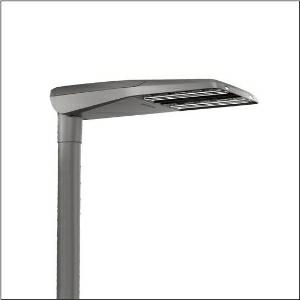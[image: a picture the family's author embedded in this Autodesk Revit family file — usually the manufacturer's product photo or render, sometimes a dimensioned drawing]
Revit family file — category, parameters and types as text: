
# Revit family: streetlight_sl_11_iq_midi___st1_2a_5xc3a41f08me_055e
name_source: partatom
category: Lighting Fixtures
units: mm (PartAtom-declared; Revit-internal decimal feet)

## family parameters
Cut with Voids When Loaded = No
Host = Face
Light Source = No
Part Type = Normal
Room Calculation Point = No
Round Connector Dimension = Use Diameter
Shared = No

## types (1)
- --- (1 x LED, 18900 lm, 124.7 W, 4000K)
    Apparent Load = 125 VA
    CIE Flux Codes = 32 70 96 100 100
    Color Rendering = 70
    Color Temperature = 4000K
    Default Elevation = 1800 mm
    Description = Streetlight SL 11 iQ midi, mast luminaire, primary light control with 3 zone facetted reflector, of plastic, silver coated, highly specular, primary optical cover: cover, of PMMA, transparent, light distribution: ST1.2a, light emission: direct distribution, primary light characteristic: asymmetric, installation type: post-top, side-entry, LED, High Power LED, rated luminous flux: 18.900lm, luminous efficacy: 152lm/W, light colour: 740, colour temperature: 4000K, control: Street-Remote, optimised constant luminous flux control (CLO 2.0), Desk-Remote (wireless, voltage-free reading and setting of iQ features in the workshop via application-optimized NFC function/RFID function), Light-Fading, Smart-Wire, Night-Set, Lumen-Switch, Temp-Guard, Auto-Match, with cable H07RN-F 5x 1.5mm², mains connection: 220..240V, AC, 50/60Hz, connection cable pre-assembled, cable length: 12,5m, start of lifetime: 125W, end of lifetime: 132W, reduction: 57W, luminaire housing, of diecast aluminium, powder-coated, Siteco® metallic grey (DB 702S), length: 780mm, width: 376mm, height: 118mm, spigot size: 60/76mm (post-top) and 42/60/76mm (side-entry), mast flange for spigot size: 42mm: 5XC10008XM4, 60mm: 5XC10008XM2, 76/60mm: 5XC10108XM1, equipment: Power, protection rating (complete): IP66, insulation class (complete): insulation class II (safety insulation), certification: CE, ENEC, VDE, impact resistance: IK09, permissible operating ambient temperature for outdoor applications: -25..+50°C, standard-compliant lighting for roads and squares, packaging unit: 1 piece

Light Distribution: ST1.2a
    Height = 118 mm
    Lamp = 1 x LED
    Lamp Light Flux = 18900 lm
    Lamp Power = 124.7 W
    Lamp count = 1
    Length = 780 mm
    Luminous efficacy = 152 lm/W
    Manufacturer = Siteco
    ModVariant = No
    Model = 5XC3A41F08ME
    Number of Poles = 1
    OnlyDefault = Yes
    Power Factor = 1
    Product Name = Streetlight SL 11 iQ midi | ST1.2a
    Product group = mast luminaire | pylon top
    ProductGroupID = 6100
    Protection Class = Protection class II
    Protection Degree = IP 66
    RLX_Detail_Level = 1
    RlxData = <blob elided: 70373 chars, md5=dbb3146e>
    Socket = socket
    Standby Power = 0 W
    System Light Flux = 18900 lm
    System Power = 125 W
    Type Comments = factory setting: luminous flux: 100 % | dim-lin: 254 | 557 mA
    Type Image = l_1005960.jpg
    URL = http://relux.com
    VarID = @adj_119001
    Voltage = 0 V
    Weight = 0.00 kg
    Width = 376 mm

## geometry (parser evidence)
native form markers: Blend x4, Sweep x10
no freeform markers — native parametric forms only
